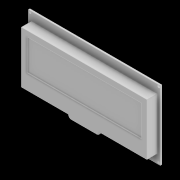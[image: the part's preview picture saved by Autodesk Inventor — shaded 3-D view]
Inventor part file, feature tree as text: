
AUTODESK INVENTOR PART (.ipt)
format: ipt  version: 2020 (Build 240168000, 168)  size: 140,800 bytes
history: native  units: in
note: dims shown in document units (in); Inventor stores cm internally (conversion verified against a paired STEP export)
features: extrude x3, other x2, fillet x2, hole x1
ambient origin geometry x8: Origin, YZ Plane, XZ Plane, XY Plane, X Axis, Y Axis, Z Axis, Center Point
bodies: Solid1 (feature_tree)
feature tree (8):
  other  "TopProfile"
  extrude  "BoardFeature"  Depth=2.625in
  extrude  "ScreenFeature"  Depth=1.375in
  extrude  "DisplayFeature"  Depth=1.0313in
  fillet  "BezelFilletsFeature"  Radius=2.5in
  fillet  "BottomFilletsFeature"  Radius=0.0625in
  hole  "MountHolesFeature"  [1 undecoded]
  other  "MountHoles"
note: 1 required parameter value undecoded (feature->parameter linkage not recoverable at this tier; creation-order binding heuristic only, values carry confidence <= 0.55)
